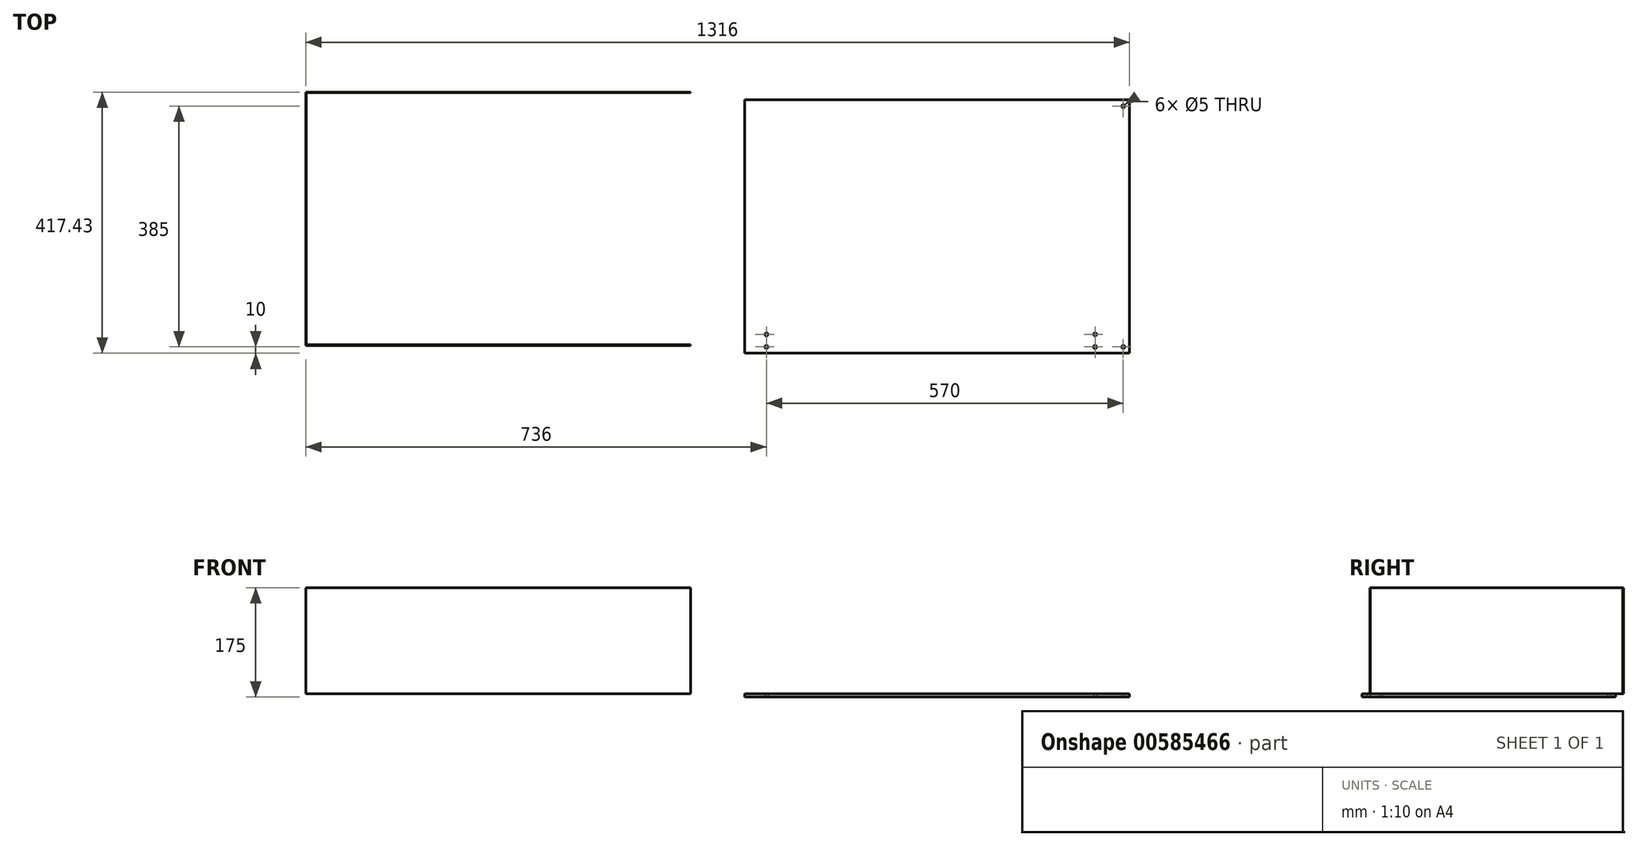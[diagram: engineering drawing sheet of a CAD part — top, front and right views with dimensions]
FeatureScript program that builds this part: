
annotation { "Feature Type Name" : "Feature", "Feature Type Description" : "" }
export const myFeature = defineFeature(function(context is Context, id is Id, definition is map)
    precondition{}
    {
        {
            var Q0;
            Q0=qCreatedBy(makeId("Top.planeOp"),FACE);
            var sketch = newSketch(context, id + "F0", { "sketchPlane" : qUnion([Q0])});
            skLineSegment(sketch, "E0.bottom", {"start": v(307.5, -202.5) * mm, "end": v(-307.5, -202.5) * mm});
            skLineSegment(sketch, "E0.top", {"start": v(307.5, 202.5) * mm, "end": v(-307.5, 202.5) * mm});
            skLineSegment(sketch, "E0.left", {"start": v(307.5, -202.5) * mm, "end": v(307.5, 202.5) * mm});
            skLineSegment(sketch, "E0.right", {"start": v(-307.5, -202.5) * mm, "end": v(-307.5, 202.5) * mm});
            skPoint(sketch, "E0.middle", {"position": v(0, 0) * mm});
            skSolve(sketch);
        }
        {
            var Q0;
            Q0=makeQuery(id+"F0.imprint","IMPRINT",FACE,{"disambiguationData":[TD([[makeQuery(id+"F0.imprint","IMPRINT",EDGE,{"derivedFrom":sQuery(id+"F0.wireOp",EDGE,"E0.bottom")}),-1.0]])]});
            extrude(context, id + "F1", {"entities" : qUnion([Q0]), "depth" : 5 * mm, "offsetDistance" : 25 * mm});
        }
        {
            var Q0;
            Q0=makeQuery(id+"F1.opExtrude","CAP_FACE",FACE,{"disambiguationData":[OSD([sQuery(id+"F0.wireOp",EDGE,"E0.bottom"),sQuery(id+"F0.wireOp",EDGE,"E0.top"),sQuery(id+"F0.wireOp",EDGE,"E0.left"),sQuery(id+"F0.wireOp",EDGE,"E0.right")])],"isStart":false});
            var sketch = newSketch(context, id + "F2", { "sketchPlane" : qUnion([Q0])});
            skLineSegment(sketch, "E1", {"start": v(-307.5, 201.5) * mm, "end": v(306.5, 201.5) * mm});
            skLineSegment(sketch, "E2", {"start": v(306.5, 201.5) * mm, "end": v(306.5, -201.5) * mm});
            skLineSegment(sketch, "E3", {"start": v(306.5, -201.5) * mm, "end": v(-307.5, -201.5) * mm});
            skLineSegment(sketch, "E4", {"start": v(-307.5, -201.5) * mm, "end": v(-307.5, -202.5) * mm});
            skLineSegment(sketch, "E5", {"start": v(-307.5, -202.5) * mm, "end": v(307.5, -202.5) * mm});
            skLineSegment(sketch, "E6", {"start": v(307.5, -202.5) * mm, "end": v(307.5, 202.5) * mm});
            skLineSegment(sketch, "E7", {"start": v(307.5, 202.5) * mm, "end": v(-307.5, 202.5) * mm});
            skLineSegment(sketch, "E8", {"start": v(-307.5, 202.5) * mm, "end": v(-307.5, 201.5) * mm});
            skSolve(sketch);
        }
        {
            var Q0;
            {var subQ0=sQuery(id+"F2.wireOp",EDGE,"E1");Q0=makeQuery(id+"F2.imprint","IMPRINT",FACE,{"disambiguationData":[TD([[makeQuery(id+"F2.imprint","IMPRINT",EDGE,{"derivedFrom":subQ0}),-1.0]])]});}
            var sketch = newSketch(context, id + "F3", { "sketchPlane" : qUnion([Q0])});
            skLineSegment(sketch, "E9", {"start": v(-393.5, -190.07) * mm, "end": v(-1008.5, -190.07) * mm});
            skLineSegment(sketch, "E10", {"start": v(-1008.5, -190.07) * mm, "end": v(-1008.5, 214.93) * mm});
            skLineSegment(sketch, "E11", {"start": v(-1008.5, 214.93) * mm, "end": v(-393.5, 214.93) * mm});
            skLineSegment(sketch, "E12", {"start": v(-393.5, 214.93) * mm, "end": v(-393.5, 213.93) * mm});
            skLineSegment(sketch, "E13", {"start": v(-393.5, 213.93) * mm, "end": v(-1007.5, 213.93) * mm});
            skLineSegment(sketch, "E14", {"start": v(-1007.5, 213.93) * mm, "end": v(-1007.5, -189.07) * mm});
            skLineSegment(sketch, "E15", {"start": v(-1007.5, -189.07) * mm, "end": v(-393.5, -189.07) * mm});
            skLineSegment(sketch, "E16", {"start": v(-393.5, -189.07) * mm, "end": v(-393.5, -190.07) * mm});
            skSolve(sketch);
        }
        {
            var Q0;
            Q0 = qSketchRegion(id + "F3", true);
            extrude(context, id + "F4", {"entities" : qUnion([Q0]), "depth" : 170 * mm, "offsetDistance" : 25 * mm});
        }
        {
            var Q0;
            Q0=makeQuery(id+"F1.opExtrude","CAP_FACE",FACE,{"disambiguationData":[OSD([sQuery(id+"F0.wireOp",EDGE,"E0.bottom"),sQuery(id+"F0.wireOp",EDGE,"E0.top"),sQuery(id+"F0.wireOp",EDGE,"E0.left"),sQuery(id+"F0.wireOp",EDGE,"E0.right")])],"isStart":true});
            var sketch = newSketch(context, id + "F5", { "sketchPlane" : qUnion([Q0])});
            skLineSegment(sketch, "E17", {"start": v(-272.5, 202.5) * mm, "end": v(-272.5, 173.6) * mm});
            skPoint(sketch, "E18", {"position": v(-272.5, 192.5) * mm});
            skSolve(sketch);
        }
        {
            var Q0;
            Q0=sQuery(id+"F5.wireOp",VERTEX,"E18");
            var Q1;
            Q1=makeQuery(id+"F1.opExtrude","SWEPT_BODY",BODY,{"disambiguationData":[OSD([sQuery(id+"F0.wireOp",EDGE,"E0.bottom"),sQuery(id+"F0.wireOp",EDGE,"E0.top"),sQuery(id+"F0.wireOp",EDGE,"E0.left"),sQuery(id+"F0.wireOp",EDGE,"E0.right")])]});
            hole(context, id + "F6", {"style" : HoleStyle.SIMPLE, "endStyle" : HoleEndStyle.THROUGH, "holeDiameter" : 5 * mm, "majorDiameter" : 5 * mm, "isTappedThrough" : true, "tappedDepth" : 12 * mm, "tapClearance" : 3, "locations" : qUnion([Q0]), "scope" : qUnion([Q1])});
        }
        {
            var Q0;
            Q0=makeQuery(id+"F1.opExtrude","CAP_FACE",FACE,{"disambiguationData":[OSD([sQuery(id+"F0.wireOp",EDGE,"E0.bottom"),sQuery(id+"F0.wireOp",EDGE,"E0.top"),sQuery(id+"F0.wireOp",EDGE,"E0.left"),sQuery(id+"F0.wireOp",EDGE,"E0.right")])],"isStart":true});
            var sketch = newSketch(context, id + "F7", { "sketchPlane" : qUnion([Q0])});
            skLineSegment(sketch, "E19", {"start": v(-272.5, 202.5) * mm, "end": v(-272.5, 172.5) * mm});
            skSolve(sketch);
        }
        {
            var Q0;
            Q0=sQuery(id+"F7.wireOp",VERTEX,"E19.end");
            var Q1;
            Q1=makeQuery(id+"F1.opExtrude","SWEPT_BODY",BODY,{"disambiguationData":[OSD([sQuery(id+"F0.wireOp",EDGE,"E0.bottom"),sQuery(id+"F0.wireOp",EDGE,"E0.top"),sQuery(id+"F0.wireOp",EDGE,"E0.left"),sQuery(id+"F0.wireOp",EDGE,"E0.right")])]});
            hole(context, id + "F8", {"style" : HoleStyle.SIMPLE, "endStyle" : HoleEndStyle.THROUGH, "holeDiameter" : 5 * mm, "majorDiameter" : 5 * mm, "isTappedThrough" : true, "tappedDepth" : 12 * mm, "tapClearance" : 3, "locations" : qUnion([Q0]), "scope" : qUnion([Q1])});
        }
        {
            var Q0;
            Q0=makeQuery(id+"F1.opExtrude","CAP_FACE",FACE,{"disambiguationData":[OSD([sQuery(id+"F0.wireOp",EDGE,"E0.bottom"),sQuery(id+"F0.wireOp",EDGE,"E0.top"),sQuery(id+"F0.wireOp",EDGE,"E0.left"),sQuery(id+"F0.wireOp",EDGE,"E0.right")])],"isStart":true});
            var sketch = newSketch(context, id + "F9", { "sketchPlane" : qUnion([Q0])});
            skLineSegment(sketch, "E20", {"start": v(252.5, 202.5) * mm, "end": v(252.5, 192.5) * mm});
            skSolve(sketch);
        }
        {
            var Q0;
            Q0=sQuery(id+"F9.wireOp",VERTEX,"E20.end");
            var Q1;
            Q1=makeQuery(id+"F1.opExtrude","SWEPT_BODY",BODY,{"disambiguationData":[OSD([sQuery(id+"F0.wireOp",EDGE,"E0.bottom"),sQuery(id+"F0.wireOp",EDGE,"E0.top"),sQuery(id+"F0.wireOp",EDGE,"E0.left"),sQuery(id+"F0.wireOp",EDGE,"E0.right")])]});
            hole(context, id + "F10", {"style" : HoleStyle.SIMPLE, "endStyle" : HoleEndStyle.THROUGH, "holeDiameter" : 5 * mm, "majorDiameter" : 5 * mm, "isTappedThrough" : true, "tappedDepth" : 12 * mm, "tapClearance" : 3, "locations" : qUnion([Q0]), "scope" : qUnion([Q1])});
        }
        {
            var Q0;
            Q0=makeQuery(id+"F1.opExtrude","CAP_FACE",FACE,{"disambiguationData":[OSD([sQuery(id+"F0.wireOp",EDGE,"E0.bottom"),sQuery(id+"F0.wireOp",EDGE,"E0.top"),sQuery(id+"F0.wireOp",EDGE,"E0.left"),sQuery(id+"F0.wireOp",EDGE,"E0.right")])],"isStart":true});
            var sketch = newSketch(context, id + "F11", { "sketchPlane" : qUnion([Q0])});
            skLineSegment(sketch, "E21", {"start": v(252.5, 202.5) * mm, "end": v(252.5, 172.5) * mm});
            skSolve(sketch);
        }
        {
            var Q0;
            Q0=sQuery(id+"F11.wireOp",VERTEX,"E21.end");
            var Q1;
            Q1=makeQuery(id+"F1.opExtrude","SWEPT_BODY",BODY,{"disambiguationData":[OSD([sQuery(id+"F0.wireOp",EDGE,"E0.bottom"),sQuery(id+"F0.wireOp",EDGE,"E0.top"),sQuery(id+"F0.wireOp",EDGE,"E0.left"),sQuery(id+"F0.wireOp",EDGE,"E0.right")])]});
            hole(context, id + "F12", {"style" : HoleStyle.SIMPLE, "endStyle" : HoleEndStyle.THROUGH, "holeDiameter" : 5 * mm, "majorDiameter" : 5 * mm, "isTappedThrough" : true, "tappedDepth" : 12 * mm, "tapClearance" : 3, "locations" : qUnion([Q0]), "scope" : qUnion([Q1])});
        }
        {
            var Q0;
            Q0=makeQuery(id+"F1.opExtrude","CAP_FACE",FACE,{"disambiguationData":[OSD([sQuery(id+"F0.wireOp",EDGE,"E0.bottom"),sQuery(id+"F0.wireOp",EDGE,"E0.top"),sQuery(id+"F0.wireOp",EDGE,"E0.left"),sQuery(id+"F0.wireOp",EDGE,"E0.right")])],"isStart":true});
            var sketch = newSketch(context, id + "F13", { "sketchPlane" : qUnion([Q0])});
            skLineSegment(sketch, "E22", {"start": v(297.5, -202.5) * mm, "end": v(297.5, -192.5) * mm});
            skSolve(sketch);
        }
        {
            var Q0;
            Q0=sQuery(id+"F13.wireOp",VERTEX,"E22.end");
            var Q1;
            Q1=makeQuery(id+"F1.opExtrude","SWEPT_BODY",BODY,{"disambiguationData":[OSD([sQuery(id+"F0.wireOp",EDGE,"E0.bottom"),sQuery(id+"F0.wireOp",EDGE,"E0.top"),sQuery(id+"F0.wireOp",EDGE,"E0.left"),sQuery(id+"F0.wireOp",EDGE,"E0.right")])]});
            hole(context, id + "F14", {"style" : HoleStyle.SIMPLE, "endStyle" : HoleEndStyle.THROUGH, "holeDiameter" : 5 * mm, "majorDiameter" : 5 * mm, "isTappedThrough" : true, "tappedDepth" : 12 * mm, "tapClearance" : 3, "locations" : qUnion([Q0]), "scope" : qUnion([Q1])});
        }
        {
            var Q0;
            Q0=makeQuery(id+"F1.opExtrude","CAP_FACE",FACE,{"disambiguationData":[OSD([sQuery(id+"F0.wireOp",EDGE,"E0.bottom"),sQuery(id+"F0.wireOp",EDGE,"E0.top"),sQuery(id+"F0.wireOp",EDGE,"E0.left"),sQuery(id+"F0.wireOp",EDGE,"E0.right")])],"isStart":true});
            var sketch = newSketch(context, id + "F15", { "sketchPlane" : qUnion([Q0])});
            skLineSegment(sketch, "E23", {"start": v(297.5, 202.5) * mm, "end": v(297.5, 192.5) * mm});
            skSolve(sketch);
        }
        {
            var Q0;
            Q0=sQuery(id+"F15.wireOp",VERTEX,"E23.end");
            var Q1;
            Q1=makeQuery(id+"F1.opExtrude","SWEPT_BODY",BODY,{"disambiguationData":[OSD([sQuery(id+"F0.wireOp",EDGE,"E0.bottom"),sQuery(id+"F0.wireOp",EDGE,"E0.top"),sQuery(id+"F0.wireOp",EDGE,"E0.left"),sQuery(id+"F0.wireOp",EDGE,"E0.right")])]});
            hole(context, id + "F16", {"style" : HoleStyle.SIMPLE, "endStyle" : HoleEndStyle.THROUGH, "holeDiameter" : 5 * mm, "majorDiameter" : 5 * mm, "isTappedThrough" : true, "tappedDepth" : 12 * mm, "tapClearance" : 3, "locations" : qUnion([Q0]), "scope" : qUnion([Q1])});
        }
    });
